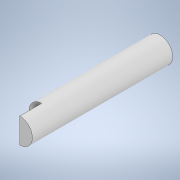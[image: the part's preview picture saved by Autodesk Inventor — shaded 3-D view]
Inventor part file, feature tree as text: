
AUTODESK INVENTOR PART (.ipt)
format: ipt  version: 2022 (Build 260153000, 153)  size: 125,952 bytes
history: mixed  units: mm
features: extrude x4, sketch x4, other x1, imported_body x1
ambient origin geometry x8: Origin, YZ Plane, XZ Plane, XY Plane, X Axis, Y Axis, Z Axis, Center Point
bodies: Solid1 (imported_parasolid)
feature tree (10):
  extrude  "Extrusion1"  Depth=20.4mm TaperAngle=0.0deg
  extrude  "Extrusion2"  Depth=4.325mm TaperAngle=0.0deg
  extrude  "Extrusion3"  [1 undecoded]
  extrude  "Extrusion4"  [1 undecoded]
  sketch  "Sketch1"  dims[d0=254.0mm d1=0.0mm d2=20.4mm d3=0.0mm]
  sketch  "Sketch2"  dims[d4=2.5mm d5=0.0mm d6=4.325mm d7=0.0mm]
  sketch  "Sketch3"
  sketch  "Sketch4"
  other  "Boss-Extrude1"
  imported_body  NMx_Import_Brep_tag  [imported B-rep: ~5 faces, bbox_mm=[2.5, 5.0, 27.9]]
note: 2 required parameter values undecoded (feature->parameter linkage not recoverable at this tier; creation-order binding heuristic only, values carry confidence <= 0.55)
